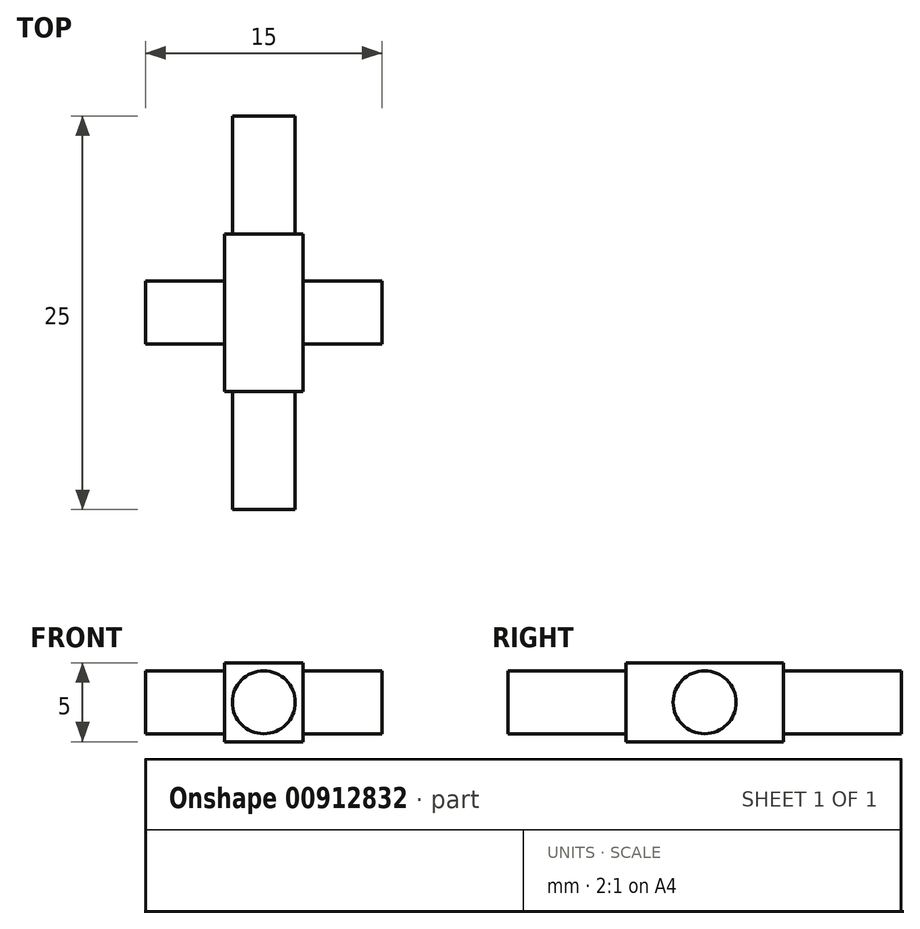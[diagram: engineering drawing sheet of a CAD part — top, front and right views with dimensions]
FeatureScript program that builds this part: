
annotation { "Feature Type Name" : "Feature", "Feature Type Description" : "" }
export const myFeature = defineFeature(function(context is Context, id is Id, definition is map)
    precondition{}
    {
        {
            var Q0;
            Q0=qCreatedBy(makeId("Top.planeOp"),FACE);
            var sketch = newSketch(context, id + "F0", { "sketchPlane" : qUnion([Q0])});
            skLineSegment(sketch, "E0.bottom", {"start": v(2.5, 5) * mm, "end": v(-2.5, 5) * mm});
            skLineSegment(sketch, "E0.top", {"start": v(2.5, -5) * mm, "end": v(-2.5, -5) * mm});
            skLineSegment(sketch, "E0.left", {"start": v(2.5, 5) * mm, "end": v(2.5, -5) * mm});
            skLineSegment(sketch, "E0.right", {"start": v(-2.5, 5) * mm, "end": v(-2.5, -5) * mm});
            skPoint(sketch, "E0.middle", {"position": v(0, 0) * mm});
            skSolve(sketch);
        }
        {
            var Q0;
            Q0 = qSketchRegion(id + "F0", true);
            extrude(context, id + "F1", {"entities" : qUnion([Q0]), "endBound" : BoundingType.SYMMETRIC, "depth" : 5 * mm, "offsetDistance" : 25 * mm});
        }
        {
            var Q0;
            Q0=qCreatedBy(makeId("Front.planeOp"),FACE);
            var sketch = newSketch(context, id + "F2", { "sketchPlane" : qUnion([Q0])});
            skCircle(sketch, "E1", {"center": v(0, 0) * mm, "radius": 2 * mm});
            skSolve(sketch);
        }
        {
            var Q0;
            Q0 = qSketchRegion(id + "F2", true);
            extrude(context, id + "F3", {"entities" : qUnion([Q0]), "operationType" : NewBodyOperationType.ADD, "endBound" : BoundingType.SYMMETRIC, "depth" : 25 * mm, "offsetDistance" : 25 * mm});
        }
        {
            var Q0;
            Q0=qCreatedBy(makeId("Right.planeOp"),FACE);
            var sketch = newSketch(context, id + "F4", { "sketchPlane" : qUnion([Q0])});
            skCircle(sketch, "E2", {"center": v(0, 0) * mm, "radius": 2 * mm});
            skSolve(sketch);
        }
        {
            var Q0;
            Q0 = qSketchRegion(id + "F4", true);
            extrude(context, id + "F5", {"entities" : qUnion([Q0]), "operationType" : NewBodyOperationType.ADD, "endBound" : BoundingType.SYMMETRIC, "depth" : 15 * mm, "offsetDistance" : 25 * mm});
        }
    });
